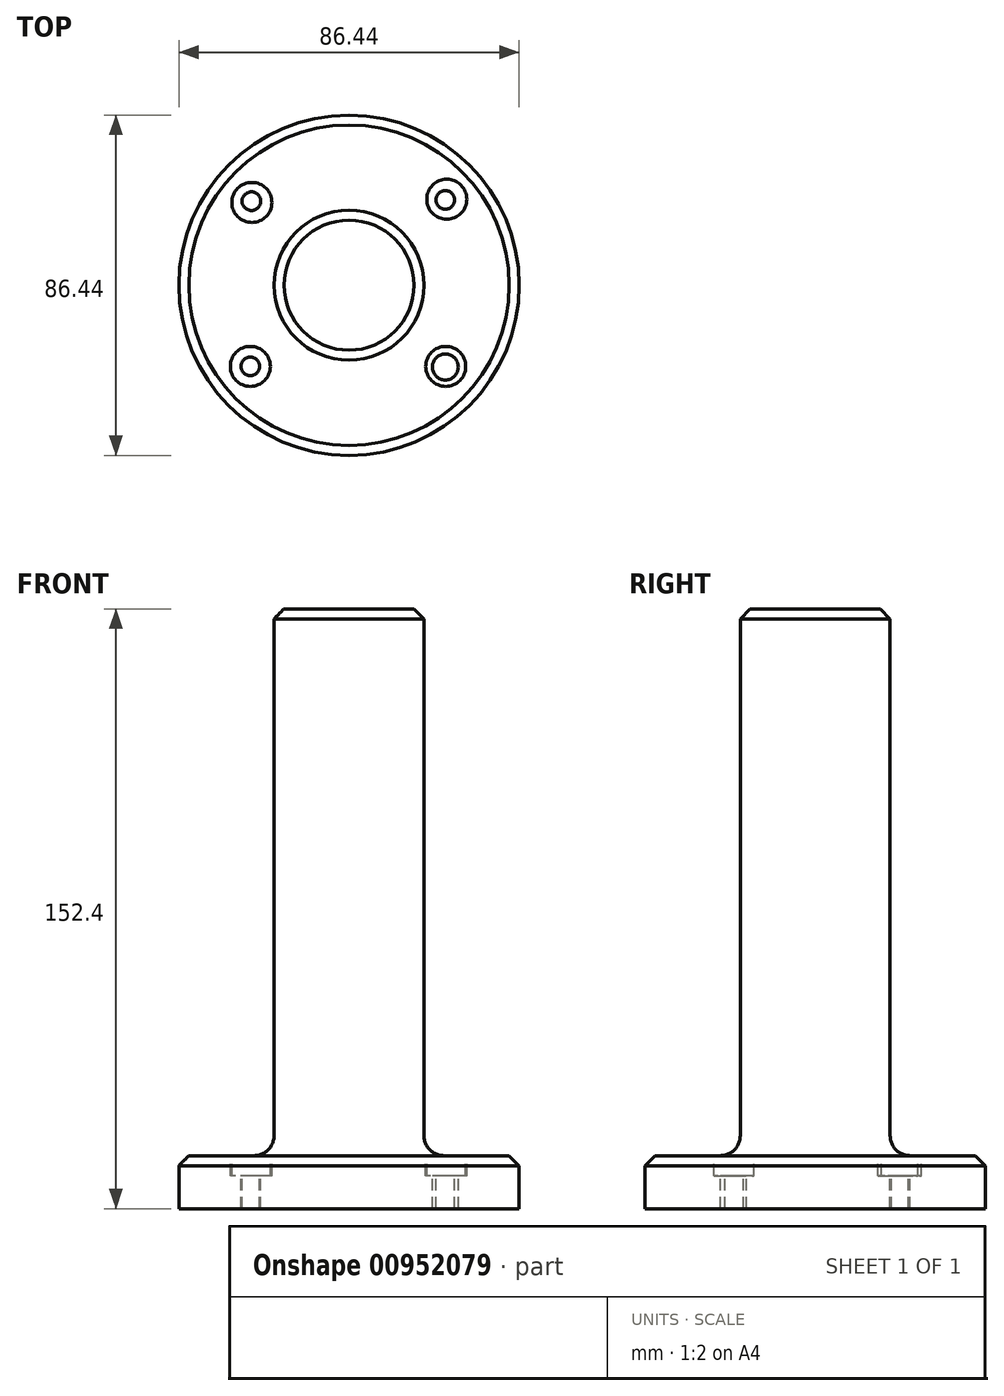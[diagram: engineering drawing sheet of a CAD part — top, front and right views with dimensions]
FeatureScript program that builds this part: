
annotation { "Feature Type Name" : "Feature", "Feature Type Description" : "" }
export const myFeature = defineFeature(function(context is Context, id is Id, definition is map)
    precondition{}
    {
        {
            var Q0;
            Q0=qCreatedBy(makeId("Front.planeOp"),FACE);
            var sketch = newSketch(context, id + "F0", { "sketchPlane" : qUnion([Q0])});
            skLineSegment(sketch, "E0.bottom", {"start": v(0, 0) * mm, "end": v(43.22, 0) * mm});
            skLineSegment(sketch, "E0.top", {"start": v(0, 13.47) * mm, "end": v(43.22, 13.47) * mm});
            skLineSegment(sketch, "E0.left", {"start": v(0, 0) * mm, "end": v(0, 13.47) * mm});
            skLineSegment(sketch, "E0.right", {"start": v(43.22, 0) * mm, "end": v(43.22, 13.47) * mm});
            skLineSegment(sketch, "E1.MirrorCS", {"start": v(-43.22, 0) * mm, "end": v(-43.22, 13.47) * mm});
            skLineSegment(sketch, "E2.MirrorCS", {"start": v(0, 13.47) * mm, "end": v(-43.22, 13.47) * mm});
            skLineSegment(sketch, "E3.MirrorCS", {"start": v(0, 0) * mm, "end": v(-43.22, 0) * mm});
            skSolve(sketch);
        }
        {
            var Q0;
            Q0=makeQuery(id+"F0.imprint","IMPRINT",FACE,{"disambiguationData":[TD([[makeQuery(id+"F0.imprint","IMPRINT",EDGE,{"derivedFrom":sQuery(id+"F0.wireOp",EDGE,"E0.bottom")}),1.0]])]});
            var Q1;
            Q1=sQuery(id+"F0.wireOp",EDGE,"E0.left");
            revolve(context, id + "F1", {"surfaceOperationType" : NewSurfaceOperationType.NEW, "entities" : qUnion([Q0]), "axis" : qUnion([Q1]), "revolveType" : RevolveType.FULL});
        }
        {
            var Q0;
            Q0=makeQuery(id+"F1.opRevolve","SWEPT_FACE",FACE,{"disambiguationData":[OSD([sQuery(id+"F0.wireOp",EDGE,"E0.bottom")])]});
            var sketch = newSketch(context, id + "F2", { "sketchPlane" : qUnion([Q0])});
            skCircle(sketch, "E4", {"center": v(0, 0) * mm, "radius": 19.05 * mm});
            skSolve(sketch);
        }
        {
            var Q0;
            Q0=makeQuery(id+"F2.imprint","IMPRINT",FACE,{"disambiguationData":[TD([[makeQuery(id+"F2.imprint","IMPRINT",EDGE,{"derivedFrom":sQuery(id+"F2.wireOp",EDGE,"E4")}),1.0]])]});
            extrude(context, id + "F3", {"entities" : qUnion([Q0]), "operationType" : NewBodyOperationType.ADD, "oppositeDirection" : true, "depth" : 152.4 * mm, "offsetDistance" : 25.4 * mm});
        }
        {
            var Q0;
            Q0=makeQuery(id+"F1.opRevolve","SWEPT_FACE",FACE,{"disambiguationData":[OSD([sQuery(id+"F0.wireOp",EDGE,"E0.top")])]});
            var sketch = newSketch(context, id + "F4", { "sketchPlane" : qUnion([Q0])});
            skLineSegment(sketch, "E5.bottom", {"start": v(-32.9, 28.03) * mm, "end": v(32.9, 28.03) * mm, "construction": true});
            skLineSegment(sketch, "E5.top", {"start": v(-32.9, -28.03) * mm, "end": v(32.9, -28.03) * mm, "construction": true});
            skLineSegment(sketch, "E5.left", {"start": v(-32.9, 28.03) * mm, "end": v(-32.9, -28.03) * mm, "construction": true});
            skLineSegment(sketch, "E5.right", {"start": v(32.9, 28.03) * mm, "end": v(32.9, -28.03) * mm, "construction": true});
            skPoint(sketch, "E5.middle", {"position": v(0, 0) * mm});
            skLineSegment(sketch, "E6", {"start": v(0, 28.03) * mm, "end": v(-32.9, 0) * mm, "construction": true});
            skLineSegment(sketch, "E7", {"start": v(-32.9, 0) * mm, "end": v(0, -28.03) * mm, "construction": true});
            skLineSegment(sketch, "E8", {"start": v(0, -28.03) * mm, "end": v(32.9, 0) * mm, "construction": true});
            skLineSegment(sketch, "E9", {"start": v(32.9, 0) * mm, "end": v(0, 28.03) * mm, "construction": true});
            skLineSegment(sketch, "E10", {"start": v(16.45, 14.02) * mm, "end": v(32.9, 28.03) * mm, "construction": true});
            skLineSegment(sketch, "E11", {"start": v(-32.9, -28.03) * mm, "end": v(-16.45, -14.02) * mm, "construction": true});
            skLineSegment(sketch, "E12", {"start": v(-16.45, 14.02) * mm, "end": v(-32.9, 28.03) * mm, "construction": true});
            skLineSegment(sketch, "E13", {"start": v(16.45, -14.02) * mm, "end": v(32.9, -28.03) * mm, "construction": true});
            skPoint(sketch, "E14", {"position": v(0, 28.03) * mm});
            skLineSegment(sketch, "E15", {"start": v(24.67, 21.02) * mm, "end": v(24.67, -21.02) * mm, "construction": true});
            skLineSegment(sketch, "E16", {"start": v(24.67, -21.02) * mm, "end": v(-24.67, -21.02) * mm, "construction": true});
            skLineSegment(sketch, "E17", {"start": v(-24.67, -21.02) * mm, "end": v(-24.67, 21.02) * mm, "construction": true});
            skLineSegment(sketch, "E18", {"start": v(-24.67, 21.02) * mm, "end": v(24.67, 21.02) * mm, "construction": true});
            skCircle(sketch, "E19", {"center": v(-24.67, 21.02) * mm, "radius": 5.08 * mm});
            skCircle(sketch, "E20", {"center": v(24.84, 21.85) * mm, "radius": 5.08 * mm});
            skCircle(sketch, "E21", {"center": v(-25.07, -20.61) * mm, "radius": 5.08 * mm});
            skCircle(sketch, "E22", {"center": v(24.57, -20.63) * mm, "radius": 5.08 * mm});
            skSolve(sketch);
        }
        {
            var Q0;
            Q0=makeQuery(id+"F4.imprint","IMPRINT",FACE,{"disambiguationData":[TD([[makeQuery(id+"F4.imprint","IMPRINT",EDGE,{"derivedFrom":sQuery(id+"F4.wireOp",EDGE,"E19")}),1.0]])]});
            var Q1;
            Q1=makeQuery(id+"F4.imprint","IMPRINT",FACE,{"disambiguationData":[TD([[makeQuery(id+"F4.imprint","IMPRINT",EDGE,{"derivedFrom":sQuery(id+"F4.wireOp",EDGE,"E20")}),1.0]])]});
            var Q2;
            Q2=makeQuery(id+"F4.imprint","IMPRINT",FACE,{"disambiguationData":[TD([[makeQuery(id+"F4.imprint","IMPRINT",EDGE,{"derivedFrom":sQuery(id+"F4.wireOp",EDGE,"E21")}),1.0]])]});
            var Q3;
            Q3=makeQuery(id+"F4.imprint","IMPRINT",FACE,{"disambiguationData":[TD([[makeQuery(id+"F4.imprint","IMPRINT",EDGE,{"derivedFrom":sQuery(id+"F4.wireOp",EDGE,"E22")}),1.0]])]});
            extrude(context, id + "F5", {"entities" : qUnion([Q0, Q1, Q2, Q3]), "operationType" : NewBodyOperationType.REMOVE, "oppositeDirection" : true, "depth" : 5.08 * mm, "offsetDistance" : 25.4 * mm});
        }
        {
            var Q0;
            Q0=makeQuery(id+"F1.opRevolve","SWEPT_FACE",FACE,{"disambiguationData":[OSD([sQuery(id+"F0.wireOp",EDGE,"E0.top")])]});
            var sketch = newSketch(context, id + "F6", { "sketchPlane" : qUnion([Q0])});
            skCircle(sketch, "E23", {"center": v(-25.07, -20.61) * mm, "radius": 2.37 * mm});
            skCircle(sketch, "E24", {"center": v(24.47, -20.76) * mm, "radius": 2.37 * mm});
            skCircle(sketch, "E25", {"center": v(24.47, 21.69) * mm, "radius": 2.37 * mm});
            skCircle(sketch, "E26", {"center": v(-24.79, 21.37) * mm, "radius": 2.37 * mm});
            skSolve(sketch);
        }
        {
            var Q0;
            Q0 = qSketchRegion(id + "F6", true);
            extrude(context, id + "F7", {"entities" : qUnion([Q0]), "operationType" : NewBodyOperationType.REMOVE, "oppositeDirection" : true, "depth" : 25.4 * mm, "offsetDistance" : 25.4 * mm});
        }
        {
            var Q0;
            Q0=makeQuery(id+"F3.opExtrude","CAP_EDGE",EDGE,{"disambiguationData":[OSD([sQuery(id+"F2.wireOp",EDGE,"E4")])],"isStart":false});
            var Q1;
            Q1=makeQuery(id+"F1.opRevolve","SWEPT_EDGE",EDGE,{"disambiguationData":[OSD([sQuery(id+"F0.wireOp",EDGE,"E0.top"),sQuery(id+"F0.wireOp",EDGE,"E0.right")])]});
            chamfer(context, id + "F8", {"entities" : qUnion([Q0, Q1]), "width" : 2.54 * mm, "tangentPropagation" : true});
        }
        {
            var Q0;
            Q0=makeQuery(id+"F3.boolean.opBoolean","INTERSECT",EDGE,{"derivedFrom":[makeQuery(id+"F1.opRevolve","SWEPT_FACE",FACE,{"disambiguationData":[OSD([sQuery(id+"F0.wireOp",EDGE,"E0.top")])]}),makeQuery(id+"F3.opExtrude","SWEPT_FACE",FACE,{"disambiguationData":[OSD([sQuery(id+"F2.wireOp",EDGE,"E4")])]})]});
            fillet(context, id + "F9", {"entities" : qUnion([Q0]), "radius" : 5.08 * mm, "tangentPropagation" : true, "allowEdgeOverflow" : false});
        }
        {
            var Q0;
            Q0=sQuery(id+"F6.wireOp",VERTEX,"E24.center");
            var Q1;
            Q1=makeQuery(id+"F1.opRevolve","SWEPT_BODY",BODY,{"disambiguationData":[OSD([sQuery(id+"F0.wireOp",EDGE,"E0.bottom"),sQuery(id+"F0.wireOp",EDGE,"E0.top"),sQuery(id+"F0.wireOp",EDGE,"E0.left"),sQuery(id+"F0.wireOp",EDGE,"E0.right")])]});
            hole(context, id + "F10", {"style" : HoleStyle.SIMPLE, "endStyle" : HoleEndStyle.THROUGH, "standardTappedOrClearance" : lookupTablePath({ "fit" : "Normal", "standard" : "ISO", "size" : "M6", "type" : "Clearance" }), "standardBlindInLast" : lookupTablePath({ "fit" : "Normal", "standard" : "ISO", "engagement" : "75%", "pitch" : "1 mm", "size" : "M6", "type" : "Clearance & tapped" }), "holeDiameter" : 6.6 * mm, "majorDiameter" : 6.35 * mm, "isTappedThrough" : true, "tappedDepth" : 12.7 * mm, "tapClearance" : 3, "locations" : qUnion([Q0]), "scope" : qUnion([Q1])});
        }
    });
